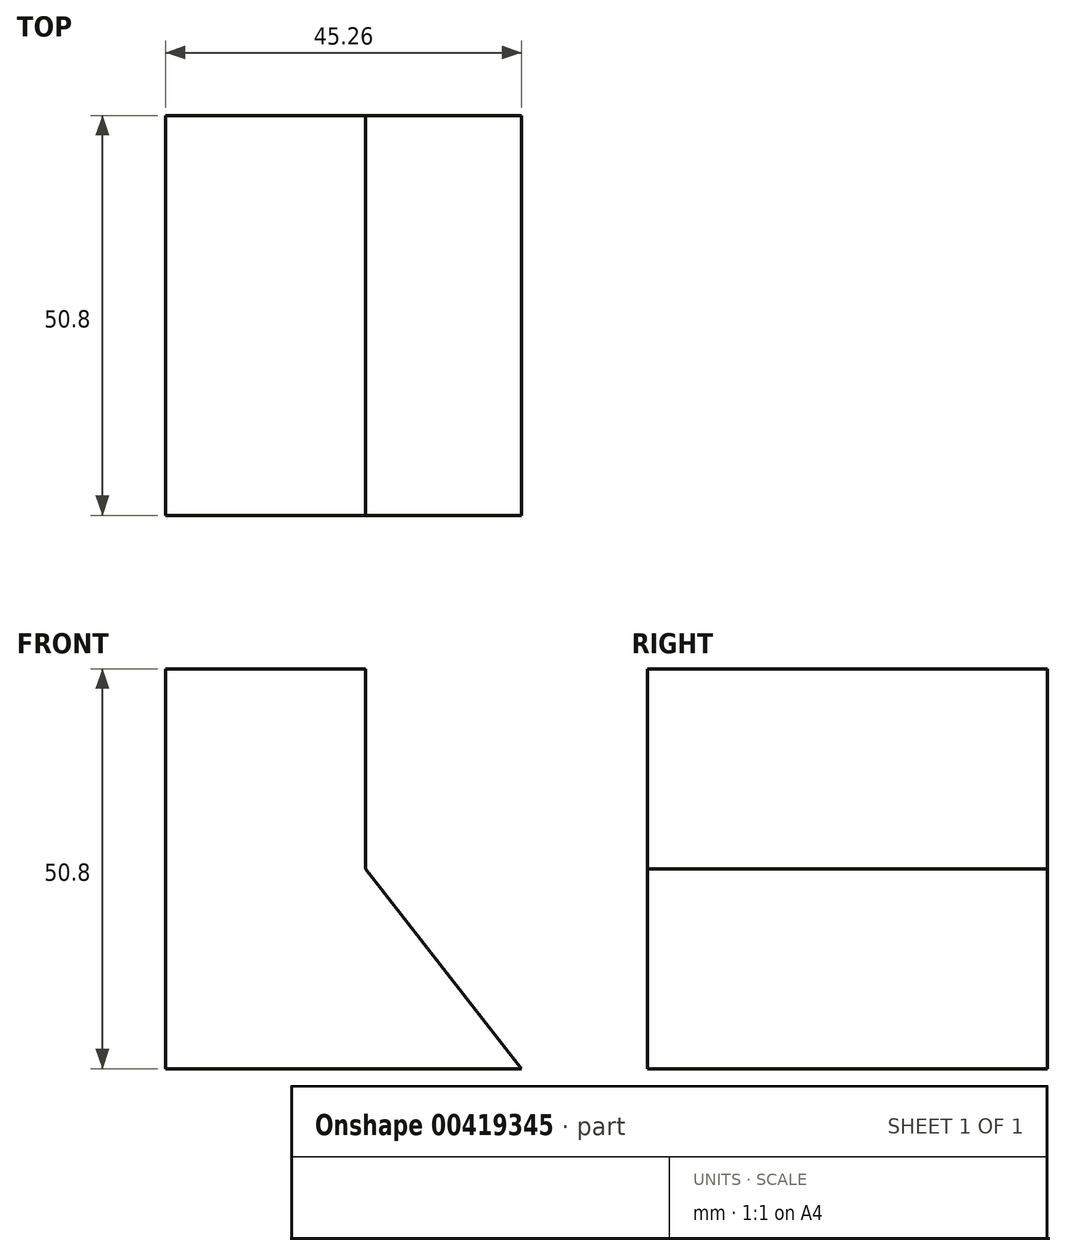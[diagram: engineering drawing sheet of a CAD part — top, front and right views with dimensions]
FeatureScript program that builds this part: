
annotation { "Feature Type Name" : "Feature", "Feature Type Description" : "" }
export const myFeature = defineFeature(function(context is Context, id is Id, definition is map)
    precondition{}
    {
        {
            var Q0;
            Q0=qCreatedBy(makeId("Front.planeOp"),FACE);
            var sketch = newSketch(context, id + "F0", { "sketchPlane" : qUnion([Q0])});
            skLineSegment(sketch, "E0", {"start": v(0, 0) * mm, "end": v(-45.26, 0) * mm});
            skLineSegment(sketch, "E1", {"start": v(-45.26, 0) * mm, "end": v(-45.26, 50.8) * mm});
            skLineSegment(sketch, "E2", {"start": v(-45.26, 50.8) * mm, "end": v(-19.86, 50.8) * mm});
            skLineSegment(sketch, "E3", {"start": v(-19.86, 50.8) * mm, "end": v(-19.86, 25.4) * mm});
            skLineSegment(sketch, "E4", {"start": v(-19.86, 25.4) * mm, "end": v(0, 0) * mm});
            skSolve(sketch);
        }
        {
            var Q0;
            Q0 = qSketchRegion(id + "F0", true);
            extrude(context, id + "F1", {"entities" : qUnion([Q0]), "depth" : 50.8 * mm});
        }
    });
